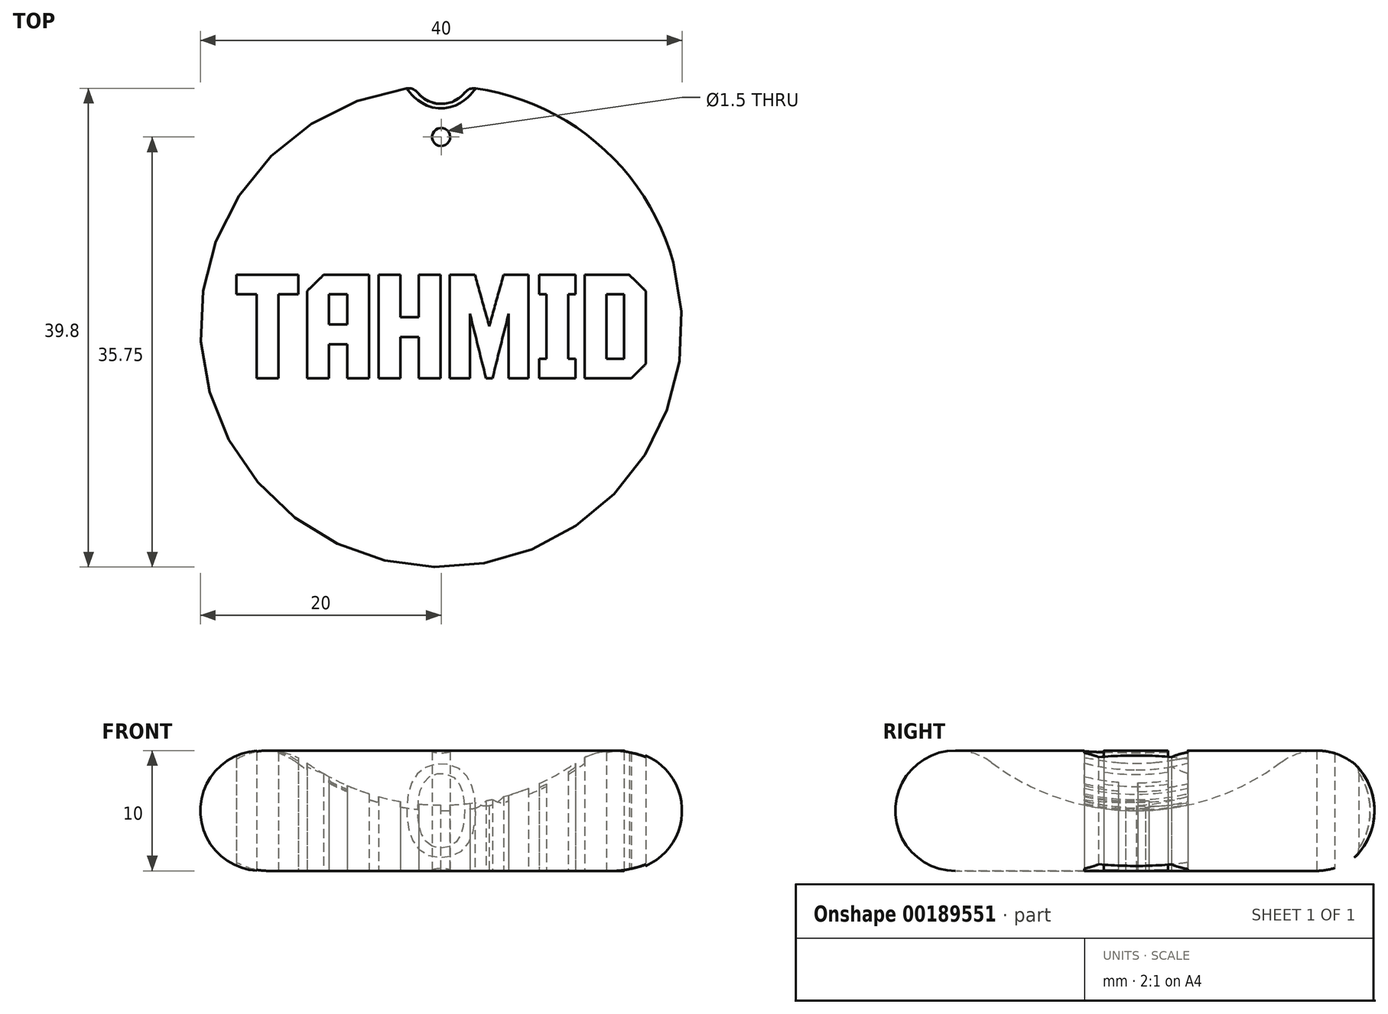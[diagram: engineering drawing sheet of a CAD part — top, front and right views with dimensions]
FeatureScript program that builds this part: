
annotation { "Feature Type Name" : "Feature", "Feature Type Description" : "" }
export const myFeature = defineFeature(function(context is Context, id is Id, definition is map)
    precondition{}
    {
        {
            var Q0;
            Q0=qCreatedBy(makeId("Front.planeOp"),FACE);
            var sketch = newSketch(context, id + "F0", { "sketchPlane" : qUnion([Q0])});
            skArc(sketch, "E0", {"start": v(-12, 9) * mm, "mid": v(-19.74, 6.58) * mm, "end": v(-15, 0) * mm});
            skArc(sketch, "E1", {"start": v(-12, 9) * mm, "mid": v(-6.32, 6.03) * mm, "end": v(0, 5) * mm});
            skLineSegment(sketch, "E2", {"start": v(-15.61, 0) * mm, "end": v(0, 0) * mm});
            skLineSegment(sketch, "E3", {"start": v(0, 0) * mm, "end": v(0, 5) * mm});
            skSolve(sketch);
        }
        {
            var Q0;
            Q0 = qSketchRegion(id + "F0", true);
            var Q1;
            Q1=sQuery(id+"F0.wireOp",EDGE,"E3");
            revolve(context, id + "F1", {"entities" : qUnion([Q0]), "axis" : qUnion([Q1]), "revolveType" : RevolveType.FULL});
        }
        {
            var Q0;
            Q0=qCreatedBy(makeId("Front.planeOp"),FACE);
            var sketch = newSketch(context, id + "F2", { "sketchPlane" : qUnion([Q0])});
            skCircle(sketch, "E4", {"center": v(-15, 5) * mm, "radius": 3.5 * mm});
            skSolve(sketch);
        }
        {
            var Q0;
            Q0 = qSketchRegion(id + "F2", true);
            var Q1;
            Q1=sQuery(id+"F0.wireOp",EDGE,"E3");
            revolve(context, id + "F3", {"operationType" : NewBodyOperationType.ADD, "entities" : qUnion([Q0]), "axis" : qUnion([Q1]), "revolveType" : RevolveType.FULL});
        }
        {
            var Q0;
            Q0=qCreatedBy(makeId("Top.planeOp"),FACE);
            var sketch = newSketch(context, id + "F4", { "sketchPlane" : qUnion([Q0])});
            skCircle(sketch, "E5", {"center": v(0, 21) * mm, "radius": 2.5 * mm});
            skSolve(sketch);
        }
        {
            var Q0;
            Q0 = qSketchRegion(id + "F4", true);
            extrude(context, id + "F5", {"entities" : qUnion([Q0]), "operationType" : NewBodyOperationType.REMOVE, "depth" : 25.4 * mm});
        }
        {
            var Q0;
            Q0=makeQuery(id+"F5.boolean.opBoolean","INTERSECT",EDGE,{"derivedFrom":[makeQuery(id+"FYrjsDwA9Br2OnP_1.boolean.opBoolean","SPLIT",FACE,{"disambiguationData":[TD([makeQuery(id+"F1.opRevolve","SWEPT_FACE",FACE,{"disambiguationData":[OSD([sQuery(id+"F0.wireOp",EDGE,"E1")])]}),makeQuery(id+"F1.opRevolve","SWEPT_FACE",FACE,{"disambiguationData":[OSD([sQuery(id+"F0.wireOp",EDGE,"E2")])]}),makeQuery(id+"FYrjsDwA9Br2OnP_1.opExtrude","SWEPT_FACE",FACE,{"disambiguationData":[OSD([sQuery(id+"Fj23RMlOwLjWWTO_1.wireOp",EDGE,"34bcf9b7-760a-4227-9f77-09c15b9400c1")])]}),makeQuery(id+"FYrjsDwA9Br2OnP_1.opExtrude","SWEPT_FACE",FACE,{"disambiguationData":[OSD([sQuery(id+"Fj23RMlOwLjWWTO_1.wireOp",EDGE,"76271fb2-3528-4823-9a9c-bac79452f4b1")])]}),makeQuery(id+"FYrjsDwA9Br2OnP_1.opExtrude","SWEPT_FACE",FACE,{"disambiguationData":[OSD([sQuery(id+"Fj23RMlOwLjWWTO_1.wireOp",EDGE,"992774ef-c71b-47fc-80f2-fca93747ac8d")])]}),makeQuery(id+"FYrjsDwA9Br2OnP_1.opExtrude","SWEPT_FACE",FACE,{"disambiguationData":[OSD([sQuery(id+"Fj23RMlOwLjWWTO_1.wireOp",EDGE,"f810fd67-dd74-48a0-8e98-82cb5b62bedf")])]}),makeQuery(id+"FYrjsDwA9Br2OnP_1.opExtrude","SWEPT_FACE",FACE,{"disambiguationData":[OSD([sQuery(id+"Fj23RMlOwLjWWTO_1.wireOp",EDGE,"9afef5d9-c2f8-41e9-a6bf-5ef68d2b0219")])]}),makeQuery(id+"FYrjsDwA9Br2OnP_1.opExtrude","SWEPT_FACE",FACE,{"disambiguationData":[OSD([sQuery(id+"Fj23RMlOwLjWWTO_1.wireOp",EDGE,"3216965c-0c1f-4878-9e29-5349ab77a6c9")])]}),makeQuery(id+"FYrjsDwA9Br2OnP_1.opExtrude","SWEPT_FACE",FACE,{"disambiguationData":[OSD([sQuery(id+"Fj23RMlOwLjWWTO_1.wireOp",EDGE,"dfa7135e-bbf4-4857-8966-0038b5322d0f")])]}),makeQuery(id+"FYrjsDwA9Br2OnP_1.opExtrude","SWEPT_FACE",FACE,{"disambiguationData":[OSD([sQuery(id+"Fj23RMlOwLjWWTO_1.wireOp",EDGE,"c10bca7b-a7a3-4d19-af3c-ca1208bea569")])]}),makeQuery(id+"FYrjsDwA9Br2OnP_1.opExtrude","SWEPT_FACE",FACE,{"disambiguationData":[OSD([sQuery(id+"Fj23RMlOwLjWWTO_1.wireOp",EDGE,"3a37f444-0f1f-4e23-9985-32a53516fc62")])]}),makeQuery(id+"FYrjsDwA9Br2OnP_1.opExtrude","SWEPT_FACE",FACE,{"disambiguationData":[OSD([sQuery(id+"Fj23RMlOwLjWWTO_1.wireOp",EDGE,"955f311a-f7ce-45a3-bae4-f725c9f22500")])]}),makeQuery(id+"FYrjsDwA9Br2OnP_1.opExtrude","SWEPT_FACE",FACE,{"disambiguationData":[OSD([sQuery(id+"Fj23RMlOwLjWWTO_1.wireOp",EDGE,"18f9f8e4-a2b2-4ffc-86b6-854a15574457")])]}),makeQuery(id+"FYrjsDwA9Br2OnP_1.opExtrude","SWEPT_FACE",FACE,{"disambiguationData":[OSD([sQuery(id+"Fj23RMlOwLjWWTO_1.wireOp",EDGE,"38a0b130-6187-41a3-a038-ce19dece9796")])]}),makeQuery(id+"FYrjsDwA9Br2OnP_1.opExtrude","SWEPT_FACE",FACE,{"disambiguationData":[OSD([sQuery(id+"Fj23RMlOwLjWWTO_1.wireOp",EDGE,"7a62a56f-93a9-4429-b9dc-28dc49b69edf")])]}),makeQuery(id+"FYrjsDwA9Br2OnP_1.opExtrude","SWEPT_FACE",FACE,{"disambiguationData":[OSD([sQuery(id+"Fj23RMlOwLjWWTO_1.wireOp",EDGE,"0bc30ca2-22b6-43f8-8032-0b5b17333202")])]}),makeQuery(id+"FYrjsDwA9Br2OnP_1.opExtrude","SWEPT_FACE",FACE,{"disambiguationData":[OSD([sQuery(id+"Fj23RMlOwLjWWTO_1.wireOp",EDGE,"502116f2-6e99-4064-879f-cf0a1462b523")])]}),makeQuery(id+"FYrjsDwA9Br2OnP_1.opExtrude","SWEPT_FACE",FACE,{"disambiguationData":[OSD([sQuery(id+"Fj23RMlOwLjWWTO_1.wireOp",EDGE,"d463303a-6914-49f0-beed-7534072399c9")])]}),makeQuery(id+"FYrjsDwA9Br2OnP_1.opExtrude","SWEPT_FACE",FACE,{"disambiguationData":[OSD([sQuery(id+"Fj23RMlOwLjWWTO_1.wireOp",EDGE,"0776bc1a-b593-4ef2-90e7-160461bc21b2")])]}),makeQuery(id+"FYrjsDwA9Br2OnP_1.opExtrude","SWEPT_FACE",FACE,{"disambiguationData":[OSD([sQuery(id+"Fj23RMlOwLjWWTO_1.wireOp",EDGE,"06d4f811-e77c-4d0b-b8e7-a9596b5f6d96")])]}),makeQuery(id+"FYrjsDwA9Br2OnP_1.opExtrude","SWEPT_FACE",FACE,{"disambiguationData":[OSD([sQuery(id+"Fj23RMlOwLjWWTO_1.wireOp",EDGE,"e1259bc6-2a12-4251-8ab2-fd89c4ff1d7b")])]}),makeQuery(id+"FYrjsDwA9Br2OnP_1.opExtrude","SWEPT_FACE",FACE,{"disambiguationData":[OSD([sQuery(id+"Fj23RMlOwLjWWTO_1.wireOp",EDGE,"32d0d525-37d2-4233-91da-ac66354d9a02")])]}),makeQuery(id+"FYrjsDwA9Br2OnP_1.opExtrude","SWEPT_FACE",FACE,{"disambiguationData":[OSD([sQuery(id+"Fj23RMlOwLjWWTO_1.wireOp",EDGE,"a80ba5f9-7976-45b9-bf08-f398d8b8330c")])]}),makeQuery(id+"FYrjsDwA9Br2OnP_1.opExtrude","SWEPT_FACE",FACE,{"disambiguationData":[OSD([sQuery(id+"Fj23RMlOwLjWWTO_1.wireOp",EDGE,"50807d5e-c4f7-47fe-b081-17c8d33a63c9")])]}),makeQuery(id+"FYrjsDwA9Br2OnP_1.opExtrude","SWEPT_FACE",FACE,{"disambiguationData":[OSD([sQuery(id+"Fj23RMlOwLjWWTO_1.wireOp",EDGE,"d2386e4a-a2c0-4486-bad9-23df067fb9d9")])]}),makeQuery(id+"FYrjsDwA9Br2OnP_1.opExtrude","SWEPT_FACE",FACE,{"disambiguationData":[OSD([sQuery(id+"Fj23RMlOwLjWWTO_1.wireOp",EDGE,"48621a8c-0fc2-4115-945c-99437912510c")])]}),makeQuery(id+"FYrjsDwA9Br2OnP_1.opExtrude","SWEPT_FACE",FACE,{"disambiguationData":[OSD([sQuery(id+"Fj23RMlOwLjWWTO_1.wireOp",EDGE,"a38bbdcd-4499-46ac-8c69-097c297fbf13")])]}),makeQuery(id+"FYrjsDwA9Br2OnP_1.opExtrude","SWEPT_FACE",FACE,{"disambiguationData":[OSD([sQuery(id+"Fj23RMlOwLjWWTO_1.wireOp",EDGE,"c1535a0d-e9e2-4dd7-8651-06d1e968b8c4")])]}),makeQuery(id+"FYrjsDwA9Br2OnP_1.opExtrude","SWEPT_FACE",FACE,{"disambiguationData":[OSD([sQuery(id+"Fj23RMlOwLjWWTO_1.wireOp",EDGE,"70fa02d1-c382-482c-bacc-599b8160de37")])]}),makeQuery(id+"FYrjsDwA9Br2OnP_1.opExtrude","SWEPT_FACE",FACE,{"disambiguationData":[OSD([sQuery(id+"Fj23RMlOwLjWWTO_1.wireOp",EDGE,"6eb8a329-5cf8-4cf4-844a-8a388277a923")])]}),makeQuery(id+"FYrjsDwA9Br2OnP_1.opExtrude","SWEPT_FACE",FACE,{"disambiguationData":[OSD([sQuery(id+"Fj23RMlOwLjWWTO_1.wireOp",EDGE,"9eb32368-581b-43d9-9df6-9822bdb82562")])]}),makeQuery(id+"FYrjsDwA9Br2OnP_1.opExtrude","SWEPT_FACE",FACE,{"disambiguationData":[OSD([sQuery(id+"Fj23RMlOwLjWWTO_1.wireOp",EDGE,"28eb79d7-6d19-4ddb-99af-b14c2f857688")])]}),makeQuery(id+"FYrjsDwA9Br2OnP_1.opExtrude","SWEPT_FACE",FACE,{"disambiguationData":[OSD([sQuery(id+"Fj23RMlOwLjWWTO_1.wireOp",EDGE,"9c20ddbe-a8f9-4692-8fc3-f3c286e4456a")])]}),makeQuery(id+"FYrjsDwA9Br2OnP_1.opExtrude","SWEPT_FACE",FACE,{"disambiguationData":[OSD([sQuery(id+"Fj23RMlOwLjWWTO_1.wireOp",EDGE,"148ea9fd-aa8d-4f05-880b-f75353e94bf5")])]})])],"derivedFrom":makeQuery(id+"F1.opRevolve","SWEPT_FACE",FACE,{"disambiguationData":[OSD([sQuery(id+"F0.wireOp",EDGE,"E0")])]})}),makeQuery(id+"F5.opExtrude","SWEPT_FACE",FACE,{"disambiguationData":[OSD([sQuery(id+"F4.wireOp",EDGE,"E5")])]})]});
            fillet(context, id + "F6", {"entities" : qUnion([Q0]), "radius" : 1 * mm, "tangentPropagation" : true, "allowEdgeOverflow" : false});
        }
        {
            var Q0;
            Q0=qCreatedBy(makeId("Top.planeOp"),FACE);
            var sketch = newSketch(context, id + "F7", { "sketchPlane" : qUnion([Q0])});
            skCircle(sketch, "E6", {"center": v(0, 15.75) * mm, "radius": 0.75 * mm});
            skSolve(sketch);
        }
        {
            var Q0;
            Q0 = qSketchRegion(id + "F7", true);
            extrude(context, id + "F8", {"entities" : qUnion([Q0]), "operationType" : NewBodyOperationType.REMOVE, "depth" : 25.4 * mm});
        }
        {
            var Q0;
            Q0=qCreatedBy(makeId("Top.planeOp"),FACE);
            var sketch = newSketch(context, id + "F9", { "sketchPlane" : qUnion([Q0])});
            skLineSegment(sketch, "E7", {"start": v(-11.88, 2.66) * mm, "end": v(-13.5, 2.66) * mm});
            skLineSegment(sketch, "E8", {"start": v(-13.5, 2.66) * mm, "end": v(-13.5, -4.3) * mm});
            skLineSegment(sketch, "E9", {"start": v(-13.5, -4.3) * mm, "end": v(-15.32, -4.3) * mm});
            skLineSegment(sketch, "E10", {"start": v(-15.32, -4.3) * mm, "end": v(-15.32, 2.66) * mm});
            skLineSegment(sketch, "E11", {"start": v(-15.32, 2.66) * mm, "end": v(-17, 2.66) * mm});
            skLineSegment(sketch, "E12", {"start": v(-17, 2.66) * mm, "end": v(-17, 4.3) * mm});
            skLineSegment(sketch, "E13", {"start": v(-17, 4.3) * mm, "end": v(-11.88, 4.3) * mm});
            skLineSegment(sketch, "E14", {"start": v(-11.88, 4.3) * mm, "end": v(-11.88, 2.66) * mm});
            skLineSegment(sketch, "E15", {"start": v(-9.34, -4.3) * mm, "end": v(-11.15, -4.3) * mm});
            skLineSegment(sketch, "E16", {"start": v(-11.15, -4.3) * mm, "end": v(-11.15, 2.94) * mm});
            skLineSegment(sketch, "E17", {"start": v(-11.15, 2.94) * mm, "end": v(-9.76, 4.3) * mm});
            skLineSegment(sketch, "E18", {"start": v(-9.76, 4.3) * mm, "end": v(-6, 4.3) * mm});
            skLineSegment(sketch, "E19", {"start": v(-6, 4.3) * mm, "end": v(-6, -4.3) * mm});
            skLineSegment(sketch, "E20", {"start": v(-6, -4.3) * mm, "end": v(-7.8, -4.3) * mm});
            skLineSegment(sketch, "E21", {"start": v(-7.8, -4.3) * mm, "end": v(-7.8, -1.48) * mm});
            skLineSegment(sketch, "E22", {"start": v(-7.8, -1.48) * mm, "end": v(-9.34, -1.48) * mm});
            skLineSegment(sketch, "E23", {"start": v(-9.34, -1.48) * mm, "end": v(-9.34, -4.3) * mm});
            skLineSegment(sketch, "E24", {"start": v(-7.8, 0.16) * mm, "end": v(-7.8, 2.66) * mm});
            skLineSegment(sketch, "E25", {"start": v(-7.8, 2.66) * mm, "end": v(-9.34, 2.66) * mm});
            skLineSegment(sketch, "E26", {"start": v(-9.34, 2.66) * mm, "end": v(-9.34, 0.16) * mm});
            skLineSegment(sketch, "E27", {"start": v(-9.34, 0.16) * mm, "end": v(-7.8, 0.16) * mm});
            skLineSegment(sketch, "E28", {"start": v(-3.4, 0.77) * mm, "end": v(-1.85, 0.77) * mm});
            skLineSegment(sketch, "E29", {"start": v(-1.85, 0.77) * mm, "end": v(-1.85, 4.3) * mm});
            skLineSegment(sketch, "E30", {"start": v(-1.85, 4.3) * mm, "end": v(-0.05, 4.3) * mm});
            skLineSegment(sketch, "E31", {"start": v(-0.05, 4.3) * mm, "end": v(-0.05, -4.3) * mm});
            skLineSegment(sketch, "E32", {"start": v(-0.05, -4.3) * mm, "end": v(-1.85, -4.3) * mm});
            skLineSegment(sketch, "E33", {"start": v(-1.85, -4.3) * mm, "end": v(-1.85, -0.86) * mm});
            skLineSegment(sketch, "E34", {"start": v(-1.85, -0.86) * mm, "end": v(-3.4, -0.86) * mm});
            skLineSegment(sketch, "E35", {"start": v(-3.4, -0.86) * mm, "end": v(-3.4, -4.3) * mm});
            skLineSegment(sketch, "E36", {"start": v(-3.4, -4.3) * mm, "end": v(-5.2, -4.3) * mm});
            skLineSegment(sketch, "E37", {"start": v(-5.2, -4.3) * mm, "end": v(-5.2, 4.3) * mm});
            skLineSegment(sketch, "E38", {"start": v(-5.2, 4.3) * mm, "end": v(-3.4, 4.3) * mm});
            skLineSegment(sketch, "E39", {"start": v(-3.4, 4.3) * mm, "end": v(-3.4, 0.77) * mm});
            skLineSegment(sketch, "E40", {"start": v(5.18, 4.3) * mm, "end": v(7.26, 4.3) * mm});
            skLineSegment(sketch, "E41", {"start": v(7.26, 4.3) * mm, "end": v(7.26, -4.3) * mm});
            skLineSegment(sketch, "E42", {"start": v(7.26, -4.3) * mm, "end": v(5.6, -4.3) * mm});
            skLineSegment(sketch, "E43", {"start": v(5.6, -4.3) * mm, "end": v(5.6, 1.05) * mm});
            skLineSegment(sketch, "E44", {"start": v(5.6, 1.05) * mm, "end": v(4.26, -4.3) * mm});
            skLineSegment(sketch, "E45", {"start": v(4.26, -4.3) * mm, "end": v(3.72, -4.3) * mm});
            skLineSegment(sketch, "E46", {"start": v(3.72, -4.3) * mm, "end": v(2.39, 1.05) * mm});
            skLineSegment(sketch, "E47", {"start": v(2.39, 1.05) * mm, "end": v(2.39, -4.3) * mm});
            skLineSegment(sketch, "E48", {"start": v(2.39, -4.3) * mm, "end": v(0.72, -4.3) * mm});
            skLineSegment(sketch, "E49", {"start": v(0.72, -4.3) * mm, "end": v(0.72, 4.3) * mm});
            skLineSegment(sketch, "E50", {"start": v(0.72, 4.3) * mm, "end": v(2.8, 4.3) * mm});
            skLineSegment(sketch, "E51", {"start": v(2.8, 4.3) * mm, "end": v(4, 0.02) * mm});
            skLineSegment(sketch, "E52", {"start": v(4, 0.02) * mm, "end": v(5.18, 4.3) * mm});
            skLineSegment(sketch, "E53", {"start": v(11.14, -2.67) * mm, "end": v(11.14, -4.3) * mm});
            skLineSegment(sketch, "E54", {"start": v(11.14, -4.3) * mm, "end": v(8.15, -4.3) * mm});
            skLineSegment(sketch, "E55", {"start": v(8.15, -4.3) * mm, "end": v(8.15, -2.67) * mm});
            skLineSegment(sketch, "E56", {"start": v(8.15, -2.67) * mm, "end": v(8.74, -2.67) * mm});
            skLineSegment(sketch, "E57", {"start": v(8.74, -2.67) * mm, "end": v(8.74, 2.67) * mm});
            skLineSegment(sketch, "E58", {"start": v(8.74, 2.67) * mm, "end": v(8.15, 2.67) * mm});
            skLineSegment(sketch, "E59", {"start": v(8.15, 2.67) * mm, "end": v(8.15, 4.3) * mm});
            skLineSegment(sketch, "E60", {"start": v(8.15, 4.3) * mm, "end": v(11.14, 4.3) * mm});
            skLineSegment(sketch, "E61", {"start": v(11.14, 4.3) * mm, "end": v(11.14, 2.67) * mm});
            skLineSegment(sketch, "E62", {"start": v(11.14, 2.67) * mm, "end": v(10.55, 2.67) * mm});
            skLineSegment(sketch, "E63", {"start": v(10.55, 2.67) * mm, "end": v(10.55, -2.67) * mm});
            skLineSegment(sketch, "E64", {"start": v(10.55, -2.67) * mm, "end": v(11.14, -2.67) * mm});
            skLineSegment(sketch, "E65", {"start": v(11.91, 4.3) * mm, "end": v(15.61, 4.3) * mm});
            skLineSegment(sketch, "E66", {"start": v(15.61, 4.3) * mm, "end": v(17, 2.94) * mm});
            skLineSegment(sketch, "E67", {"start": v(17, 2.94) * mm, "end": v(17, -3.11) * mm});
            skLineSegment(sketch, "E68", {"start": v(17, -3.11) * mm, "end": v(15.8, -4.3) * mm});
            skLineSegment(sketch, "E69", {"start": v(15.8, -4.3) * mm, "end": v(11.91, -4.3) * mm});
            skLineSegment(sketch, "E70", {"start": v(11.91, -4.3) * mm, "end": v(11.91, 4.3) * mm});
            skLineSegment(sketch, "E71", {"start": v(15.2, -2.67) * mm, "end": v(15.2, 2.66) * mm});
            skLineSegment(sketch, "E72", {"start": v(15.2, 2.66) * mm, "end": v(13.72, 2.66) * mm});
            skLineSegment(sketch, "E73", {"start": v(13.72, 2.66) * mm, "end": v(13.72, -2.67) * mm});
            skLineSegment(sketch, "E74", {"start": v(13.72, -2.67) * mm, "end": v(15.2, -2.67) * mm});
            skSolve(sketch);
        }
        {
            var Q0;
            Q0 = qSketchRegion(id + "F9", true);
            extrude(context, id + "F10", {"entities" : qUnion([Q0]), "operationType" : NewBodyOperationType.REMOVE, "depth" : 25.4 * mm});
        }
    });
